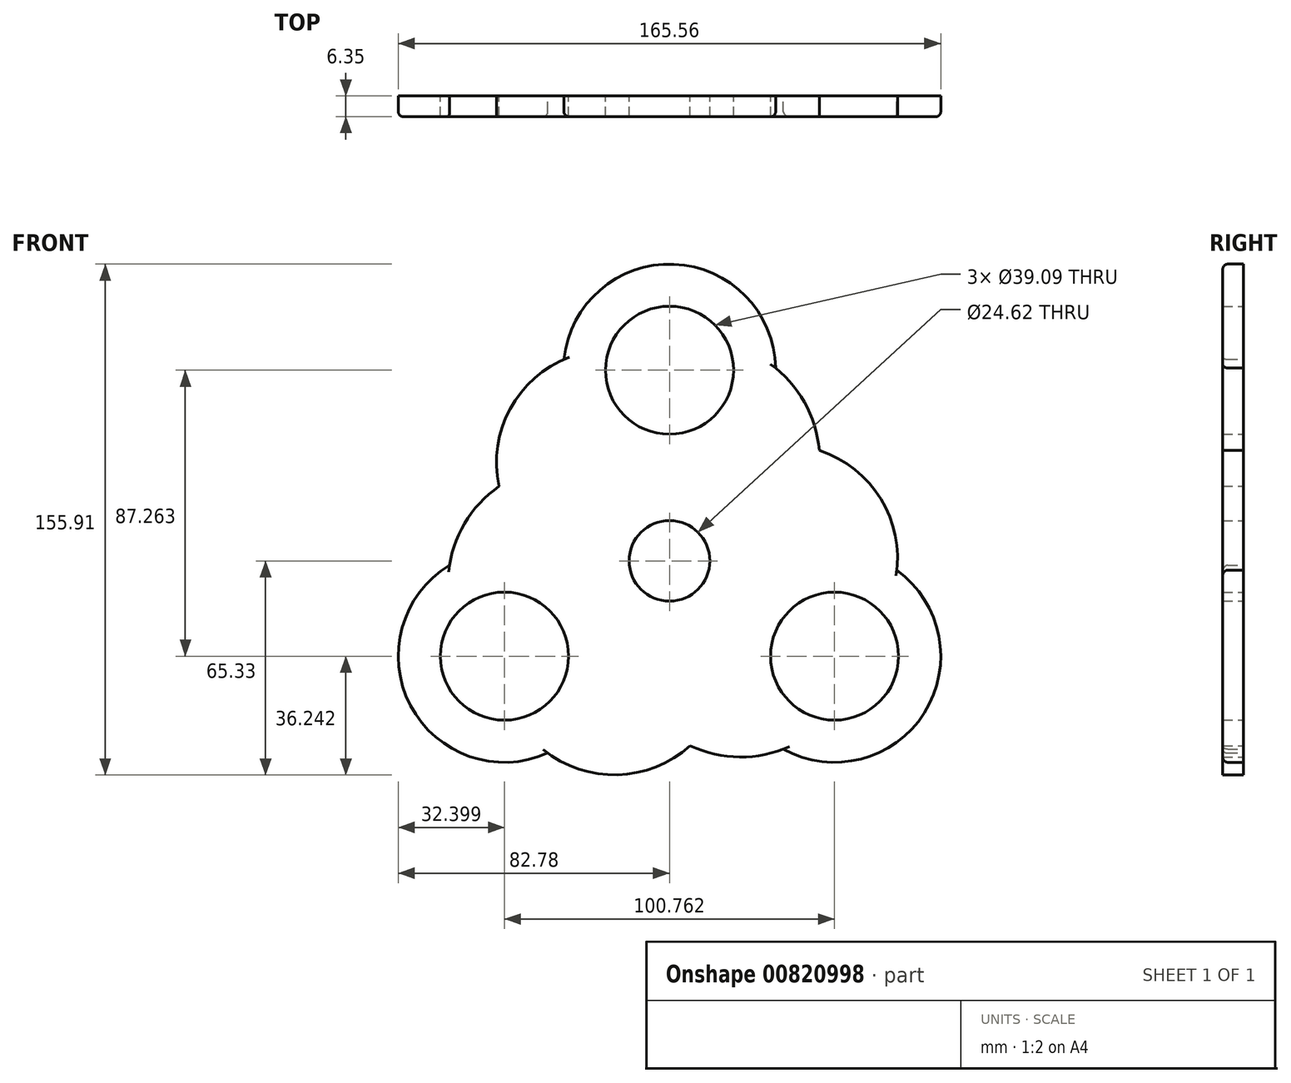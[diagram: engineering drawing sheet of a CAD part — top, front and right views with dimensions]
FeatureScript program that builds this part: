
annotation { "Feature Type Name" : "Feature", "Feature Type Description" : "" }
export const myFeature = defineFeature(function(context is Context, id is Id, definition is map)
    precondition{}
    {
        {
            var Q0;
            Q0=qCreatedBy(makeId("Front.planeOp"),FACE);
            var sketch = newSketch(context, id + "F0", { "sketchPlane" : qUnion([Q0])});
            skCircle(sketch, "E0", {"center": v(0, 0) * mm, "radius": 12.3 * mm});
            skCircle(sketch, "E1", {"center": v(0, 58.18) * mm, "radius": 19.55 * mm});
            skArc(sketch, "E2", {"start": v(32.4, 58.84) * mm, "mid": v(1.33, 90.55) * mm, "end": v(-32.23, 61.5) * mm});
            skArc(sketch, "E3", {"start": v(45.7, 33.67) * mm, "mid": v(41.61, 47.61) * mm, "end": v(32.4, 58.84) * mm});
            skArc(sketch, "E4", {"start": v(-32.23, 61.5) * mm, "mid": v(-49.03, 45.65) * mm, "end": v(-52.01, 22.75) * mm});
            skArc(sketch, "E5.1.0", {"start": v(-67.16, -1.37) * mm, "mid": v(-79.08, -44.12) * mm, "end": v(-37.14, -58.66) * mm});
            skArc(sketch, "E5.2.0", {"start": v(34.76, -57.48) * mm, "mid": v(77.75, -46.43) * mm, "end": v(69.37, -2.84) * mm});
            skCircle(sketch, "E6.1.1", {"center": v(-50.38, -29.09) * mm, "radius": 19.55 * mm});
            skArc(sketch, "E6.1.2", {"start": v(-52.01, 22.75) * mm, "mid": v(-62.04, 12.23) * mm, "end": v(-67.16, -1.37) * mm});
            skArc(sketch, "E6.1.3", {"start": v(-37.14, -58.66) * mm, "mid": v(-15.02, -65.28) * mm, "end": v(6.3, -56.42) * mm});
            skCircle(sketch, "E6.2.1", {"center": v(50.38, -29.09) * mm, "radius": 19.55 * mm});
            skArc(sketch, "E6.2.2", {"start": v(6.3, -56.42) * mm, "mid": v(20.43, -59.84) * mm, "end": v(34.76, -57.48) * mm});
            skArc(sketch, "E6.2.3", {"start": v(69.37, -2.84) * mm, "mid": v(64.04, 19.64) * mm, "end": v(45.7, 33.67) * mm});
            skPoint(sketch, "E7.orphan", {"position": v(-5.22, 18.38) * mm});
            skPoint(sketch, "E8.orphan", {"position": v(5.5, 18.3) * mm});
            skPoint(sketch, "E9.orphan", {"position": v(13.1, -13.9) * mm});
            skPoint(sketch, "E10.orphan", {"position": v(-13.3, -13.7) * mm});
            skSolve(sketch);
        }
        {
            var Q0;
            Q0=makeQuery(id+"F0.imprint","IMPRINT",FACE,{"disambiguationData":[TD([[makeQuery(id+"F0.imprint","IMPRINT",EDGE,{"derivedFrom":sQuery(id+"F0.wireOp",EDGE,"E0")}),-1.0]])]});
            extrude(context, id + "F1", {"entities" : qUnion([Q0]), "depth" : 6.35 * mm, "offsetDistance" : 25.4 * mm});
        }
        {
            var Q0;
            Q0=makeQuery(id+"F1.opExtrude","CAP_EDGE",EDGE,{"disambiguationData":[OSD([sQuery(id+"F0.wireOp",EDGE,"E2")])],"isStart":false});
            var Q1;
            Q1=makeQuery(id+"F1.opExtrude","CAP_EDGE",EDGE,{"disambiguationData":[OSD([sQuery(id+"F0.wireOp",EDGE,"E5.2.0")])],"isStart":false});
            var Q2;
            Q2=makeQuery(id+"F1.opExtrude","CAP_EDGE",EDGE,{"disambiguationData":[OSD([sQuery(id+"F0.wireOp",EDGE,"E5.1.0")])],"isStart":false});
            fillet(context, id + "F2", {"entities" : qUnion([Q0, Q1, Q2]), "radius" : 1.52 * mm, "tangentPropagation" : true, "allowEdgeOverflow" : false});
        }
    });
